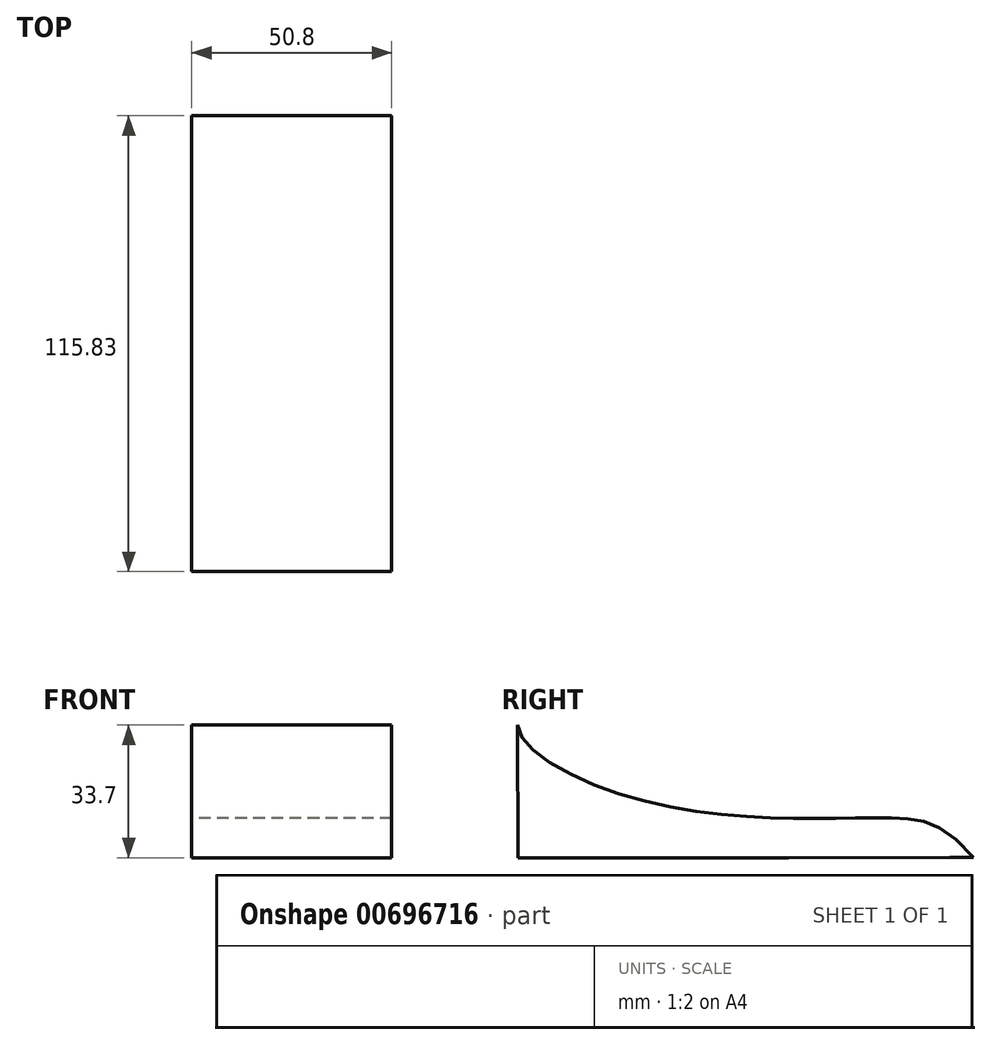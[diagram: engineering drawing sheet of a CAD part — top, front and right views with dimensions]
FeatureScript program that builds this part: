
annotation { "Feature Type Name" : "Feature", "Feature Type Description" : "" }
export const myFeature = defineFeature(function(context is Context, id is Id, definition is map)
    precondition{}
    {
        {
            var Q0;
            Q0=qCreatedBy(makeId("Right.planeOp"),FACE);
            var sketch = newSketch(context, id + "F0", { "sketchPlane" : qUnion([Q0])});
            skLineSegment(sketch, "E0", {"start": v(-54.94, -28.12) * mm, "end": v(-54.99, 5.58) * mm});
            skLineSegment(sketch, "E1", {"start": v(-54.94, -28.12) * mm, "end": v(-45.41, -28.12) * mm});
            skLineSegment(sketch, "E2", {"start": v(-20.6, -28.12) * mm, "end": v(13.83, -28.12) * mm});
            skLineSegment(sketch, "E3", {"start": v(54.84, -28.03) * mm, "end": v(60.84, -28.03) * mm});
            skFitSpline(sketch, "E4", {"points": [v(60.84, -28.03) * mm, v(39.86, -18) * mm, v(12.11, -18.06) * mm, v(-32.52, -10.74) * mm, v(-54.99, 5.58) * mm], "startDerivative": vector(-107.3, 127.56) * mm, "endDerivative": vector(-0.1, 70.2) * mm});
            skLineSegment(sketch, "E5", {"start": v(-45.41, -28.12) * mm, "end": v(-20.6, -28.12) * mm});
            skLineSegment(sketch, "E6", {"start": v(13.83, -28.12) * mm, "end": v(54.84, -28.03) * mm});
            skSolve(sketch);
        }
        {
            var Q0;
            Q0 = qSketchRegion(id + "F0", true);
            extrude(context, id + "F1", {"entities" : qUnion([Q0]), "depth" : 50.8 * mm, "offsetDistance" : 25.4 * mm});
        }
    });
